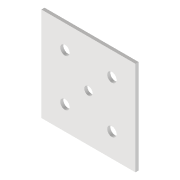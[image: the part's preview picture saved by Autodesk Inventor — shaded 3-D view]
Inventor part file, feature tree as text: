
AUTODESK INVENTOR PART (.ipt)
format: ipt  version: 2022 (Build 260153000, 153)  size: 97,792 bytes
history: native  units: mm
features: extrude x1, sketch x1
ambient origin geometry x8: Origin, YZ Plane, XZ Plane, XY Plane, X Axis, Y Axis, Z Axis, Center Point
bodies: Volumenkörper1 (feature_tree)
feature tree (2):
  extrude  "Extrusion1"  Depth=30.0mm
  sketch  "Skizze1"  dims[d0=30.0mm d1=30.0mm d2=15.0mm d3=15.0mm d4=3.0mm d5=3.0mm d6=3.0mm d7=3.0mm d8=1.0mm d9=0.0mm]
